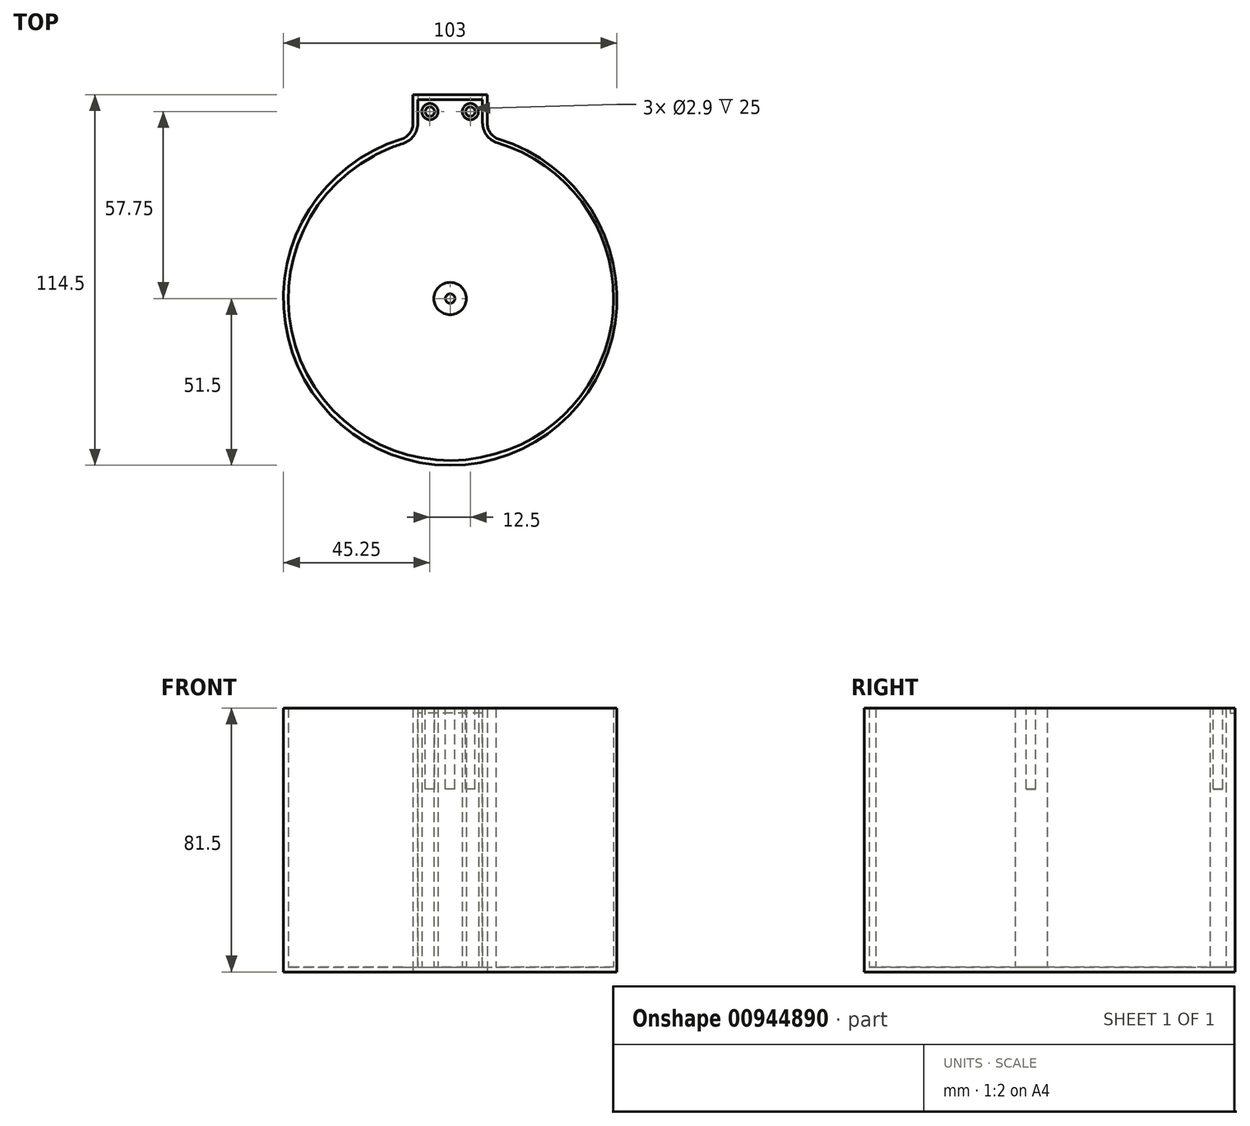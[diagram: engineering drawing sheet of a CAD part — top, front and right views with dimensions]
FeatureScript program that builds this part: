
annotation { "Feature Type Name" : "Feature", "Feature Type Description" : "" }
export const myFeature = defineFeature(function(context is Context, id is Id, definition is map)
    precondition{}
    {
        {
            var Q0;
            Q0=qCreatedBy(makeId("Top.planeOp"),FACE);
            var sketch = newSketch(context, id + "F0", { "sketchPlane" : qUnion([Q0])});
            skArc(sketch, "E0", {"start": v(-15.04, 49.25) * mm, "mid": v(0, -51.5) * mm, "end": v(15.04, 49.25) * mm});
            skArc(sketch, "E1", {"start": v(-23.6, 44.08) * mm, "mid": v(-46.27, -18.96) * mm, "end": v(14.13, -47.96) * mm});
            skCircle(sketch, "E2", {"center": v(0, 0) * mm, "radius": 10 * mm, "construction": true});
            skLineSegment(sketch, "E3", {"start": v(-10, 61.5) * mm, "end": v(10, 61.5) * mm});
            skCircle(sketch, "E4", {"center": v(0, 0) * mm, "radius": 11.5 * mm, "construction": true});
            skLineSegment(sketch, "E5", {"start": v(11.5, 54.04) * mm, "end": v(11.5, 63) * mm});
            skLineSegment(sketch, "E6", {"start": v(11.5, 63) * mm, "end": v(-11.5, 63) * mm});
            skLineSegment(sketch, "E7.trimOffspring", {"start": v(-11.5, 54.04) * mm, "end": v(-11.5, 63) * mm});
            skPoint(sketch, "E8.start.orphan", {"position": v(-11.5, 0) * mm});
            skPoint(sketch, "E9.orphan", {"position": v(11.5, 0) * mm});
            skPoint(sketch, "E10.visualSharp", {"position": v(-10, 48.99) * mm});
            skPoint(sketch, "E11.visualSharp", {"position": v(10, 48.99) * mm});
            skArc(sketch, "E11.filletArc", {"start": v(14.23, -47.93) * mm, "mid": v(14.18, -47.95) * mm, "end": v(14.13, -47.96) * mm});
            skPoint(sketch, "E12.visualSharp", {"position": v(11.5, 50.2) * mm});
            skArc(sketch, "E13", {"start": v(14.13, -47.96) * mm, "mid": v(50.5, -0.13) * mm, "end": v(14.66, 48.1) * mm});
            skLineSegment(sketch, "E14", {"start": v(15.04, 49.25) * mm, "end": v(15.04, 49.25) * mm});
            skLineSegment(sketch, "E15", {"start": v(-11.5, 54.04) * mm, "end": v(-11.5, 54.04) * mm});
            skLineSegment(sketch, "E16", {"start": v(11.5, 54.04) * mm, "end": v(11.5, 54.04) * mm});
            skLineSegment(sketch, "E17.trimOffspring", {"start": v(-15.04, 49.25) * mm, "end": v(-15.04, 49.25) * mm});
            skLineSegment(sketch, "E18.trimOffspring", {"start": v(10, 54.33) * mm, "end": v(10, 61.5) * mm});
            skPoint(sketch, "E19.start.orphan", {"position": v(10, 0) * mm});
            skPoint(sketch, "E20.start.orphan", {"position": v(-10, 0) * mm});
            skPoint(sketch, "E21.visualSharp", {"position": v(-11.5, 50.2) * mm});
            skArc(sketch, "E21.filletArc", {"start": v(-15.04, 49.25) * mm, "mid": v(-12.48, 51.06) * mm, "end": v(-11.5, 54.04) * mm});
            skArc(sketch, "E22.filletArc", {"start": v(11.5, 54.04) * mm, "mid": v(12.48, 51.06) * mm, "end": v(15.04, 49.25) * mm});
            skPoint(sketch, "E23.visualSharp", {"position": v(10, 49.23) * mm});
            skArc(sketch, "E23.filletArc", {"start": v(10, 54.33) * mm, "mid": v(11.3, 50.44) * mm, "end": v(14.66, 48.1) * mm});
            skLineSegment(sketch, "E24", {"start": v(-10, 61.5) * mm, "end": v(-10, 54.12) * mm});
            skArc(sketch, "E25.trimOffspring", {"start": v(-14.56, 47.91) * mm, "mid": v(-19.17, 46.22) * mm, "end": v(-23.6, 44.08) * mm});
            skPoint(sketch, "E26.visualSharp", {"position": v(-10, 49.1) * mm});
            skArc(sketch, "E26.filletArc", {"start": v(-14.56, 47.91) * mm, "mid": v(-11.26, 50.27) * mm, "end": v(-10, 54.12) * mm});
            skCircle(sketch, "E27", {"center": v(-6.25, 57.75) * mm, "radius": 2.5 * mm});
            skCircle(sketch, "E28.2.0.0", {"center": v(6.25, 57.75) * mm, "radius": 2.5 * mm});
            skLineSegment(sketch, "E28.direction1", {"start": v(-6.25, 57.75) * mm, "end": v(0, 57.75) * mm, "construction": true});
            skCircle(sketch, "E29", {"center": v(0, 0) * mm, "radius": 5 * mm});
            skSolve(sketch);
        }
        {
            var Q0;
            Q0=makeQuery(id+"F0.imprint","IMPRINT",FACE,{"disambiguationData":[TD([[makeQuery(id+"F0.imprint","IMPRINT",EDGE,{"derivedFrom":sQuery(id+"F0.wireOp",EDGE,"E0")}),1.0]])]});
            var Q1;
            Q1=makeQuery(id+"F0.imprint","IMPRINT",FACE,{"disambiguationData":[TD([[makeQuery(id+"F0.imprint","IMPRINT",EDGE,{"derivedFrom":sQuery(id+"F0.wireOp",EDGE,"E27")}),1.0]])]});
            var Q2;
            Q2=makeQuery(id+"F0.imprint","IMPRINT",FACE,{"disambiguationData":[TD([[makeQuery(id+"F0.imprint","IMPRINT",EDGE,{"derivedFrom":sQuery(id+"F0.wireOp",EDGE,"E28.2.0.0")}),1.0]])]});
            var Q3;
            Q3=makeQuery(id+"F0.imprint","IMPRINT",FACE,{"disambiguationData":[TD([[makeQuery(id+"F0.imprint","IMPRINT",EDGE,{"derivedFrom":sQuery(id+"F0.wireOp",EDGE,"E29")}),1.0]])]});
            extrude(context, id + "F1", {"entities" : qUnion([Q0, Q1, Q2, Q3]), "depth" : 80 * mm, "offsetDistance" : 25 * mm});
        }
        {
            var Q0;
            Q0=makeQuery(id+"F1.opExtrude","CAP_FACE",FACE,{"disambiguationData":[OSD([sQuery(id+"F0.wireOp",EDGE,"E29")])],"isStart":true});
            var sketch = newSketch(context, id + "F2", { "sketchPlane" : qUnion([Q0])});
            skArc(sketch, "E30", {"start": v(15.04, -49.25) * mm, "mid": v(0, 51.5) * mm, "end": v(-15.04, -49.25) * mm});
            skCircle(sketch, "E31", {"center": v(0, 0) * mm, "radius": 11.5 * mm, "construction": true});
            skLineSegment(sketch, "E32", {"start": v(-11.5, -54.04) * mm, "end": v(-11.5, -63) * mm});
            skLineSegment(sketch, "E33", {"start": v(-11.5, -63) * mm, "end": v(11.5, -63) * mm});
            skPoint(sketch, "E34.orphan", {"position": v(11.92, 0) * mm});
            skLineSegment(sketch, "E35", {"start": v(11.5, -54.04) * mm, "end": v(11.5, -63) * mm});
            skPoint(sketch, "E36.orphan", {"position": v(-11.5, 0) * mm});
            skPoint(sketch, "E37.orphan", {"position": v(11.5, 0) * mm});
            skPoint(sketch, "E38.visualSharp", {"position": v(-11.5, -50.2) * mm});
            skArc(sketch, "E38.filletArc", {"start": v(-11.5, -54.04) * mm, "mid": v(-12.48, -51.06) * mm, "end": v(-15.04, -49.25) * mm});
            skPoint(sketch, "E39.visualSharp", {"position": v(11.5, -50.2) * mm});
            skArc(sketch, "E39.filletArc", {"start": v(15.04, -49.25) * mm, "mid": v(12.48, -51.06) * mm, "end": v(11.5, -54.04) * mm});
            skSolve(sketch);
        }
        {
            var Q0;
            Q0 = qSketchRegion(id + "F2", true);
            extrude(context, id + "F3", {"entities" : qUnion([Q0]), "operationType" : NewBodyOperationType.ADD, "depth" : 1.5 * mm, "offsetDistance" : 25 * mm});
        }
        {
            var Q0;
            Q0=makeQuery(id+"F3.boolean.opBoolean","MERGE",FACE,{"derivedFrom":[makeQuery(id+"F1.opExtrude","SWEPT_FACE",FACE,{"disambiguationData":[OSD([sQuery(id+"F0.wireOp",EDGE,"E6")])]}),makeQuery(id+"F3.opExtrude","SWEPT_FACE",FACE,{"disambiguationData":[OSD([sQuery(id+"F2.wireOp",EDGE,"E33")])]})]});
            var sketch = newSketch(context, id + "F4", { "sketchPlane" : qUnion([Q0])});
            skLineSegment(sketch, "E40.bottom", {"start": v(10, 0) * mm, "end": v(-10, 0) * mm});
            skLineSegment(sketch, "E40.top", {"start": v(10, 78.5) * mm, "end": v(-10, 78.5) * mm});
            skLineSegment(sketch, "E40.left", {"start": v(10, 0) * mm, "end": v(10, 78.5) * mm});
            skLineSegment(sketch, "E40.right", {"start": v(-10, 0) * mm, "end": v(-10, 78.5) * mm});
            skSolve(sketch);
        }
        {
            var Q0;
            Q0 = qSketchRegion(id + "F4", true);
            extrude(context, id + "F5", {"entities" : qUnion([Q0]), "operationType" : NewBodyOperationType.REMOVE, "endBound" : BoundingType.UP_TO_NEXT, "oppositeDirection" : true, "depth" : 25 * mm, "offsetDistance" : 25 * mm});
        }
        {
            var Q0;
            Q0=makeQuery(id+"F1.opExtrude","CAP_FACE",FACE,{"disambiguationData":[OSD([sQuery(id+"F0.wireOp",EDGE,"E29")])],"isStart":false});
            var sketch = newSketch(context, id + "F6", { "sketchPlane" : qUnion([Q0])});
            skCircle(sketch, "E41", {"center": v(0, 0) * mm, "radius": 1.45 * mm});
            skLineSegment(sketch, "E42", {"start": v(0, 0) * mm, "end": v(0, 57.75) * mm, "construction": true});
            skLineSegment(sketch, "E43", {"start": v(0, 57.75) * mm, "end": v(-6.25, 57.75) * mm, "construction": true});
            skLineSegment(sketch, "E44", {"start": v(0, 57.75) * mm, "end": v(6.25, 57.75) * mm, "construction": true});
            skCircle(sketch, "E45", {"center": v(-6.25, 57.75) * mm, "radius": 1.45 * mm});
            skCircle(sketch, "E46", {"center": v(6.25, 57.75) * mm, "radius": 1.45 * mm});
            skSolve(sketch);
        }
        {
            var Q0;
            Q0 = qSketchRegion(id + "F6", true);
            extrude(context, id + "F7", {"entities" : qUnion([Q0]), "operationType" : NewBodyOperationType.REMOVE, "oppositeDirection" : true, "depth" : 25 * mm, "offsetDistance" : 25 * mm});
        }
    });
